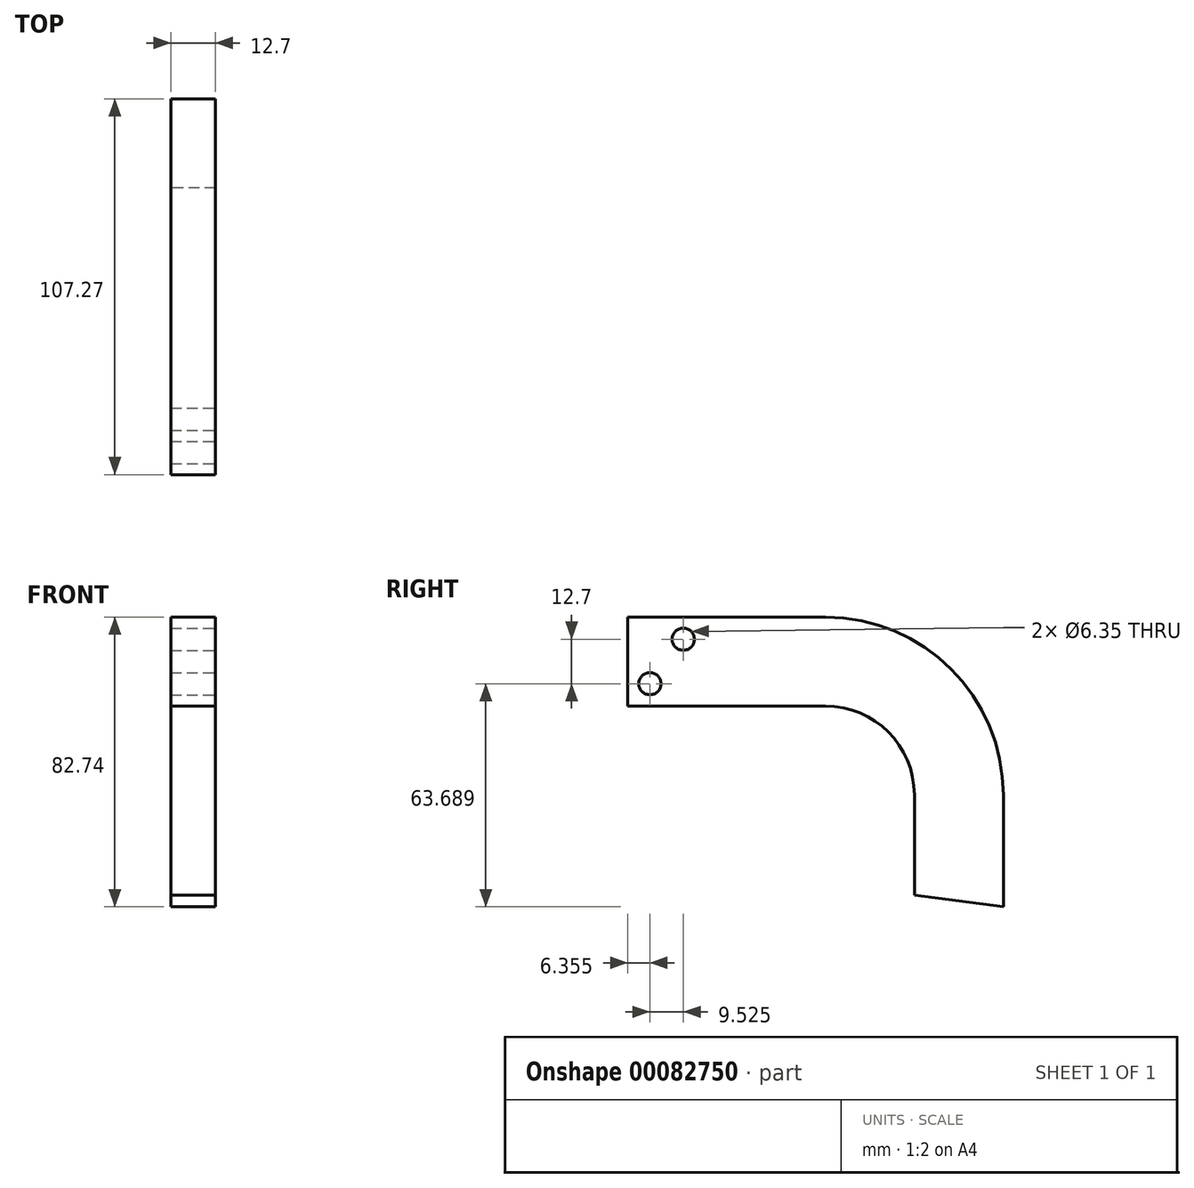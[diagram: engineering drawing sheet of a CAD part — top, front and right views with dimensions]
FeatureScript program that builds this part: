
annotation { "Feature Type Name" : "Feature", "Feature Type Description" : "" }
export const myFeature = defineFeature(function(context is Context, id is Id, definition is map)
    precondition{}
    {
        {
            var Q0;
            Q0=qCreatedBy(makeId("Right.planeOp"),FACE);
            var sketch = newSketch(context, id + "F0", { "sketchPlane" : qUnion([Q0])});
            skLineSegment(sketch, "E0.top", {"start": v(-57.14, 11.66) * mm, "end": v(-0.67, 11.66) * mm});
            skLineSegment(sketch, "E0.left", {"start": v(-57.14, 37.06) * mm, "end": v(-57.14, 11.66) * mm});
            skLineSegment(sketch, "E1", {"start": v(24.73, -13.74) * mm, "end": v(24.73, -42.32) * mm});
            skLineSegment(sketch, "E2", {"start": v(50.13, -45.68) * mm, "end": v(24.73, -42.32) * mm});
            skPoint(sketch, "E3.visualSharp", {"position": v(24.73, 11.66) * mm});
            skArc(sketch, "E3.filletArc", {"start": v(24.73, -13.74) * mm, "mid": v(17.29, 4.22) * mm, "end": v(-0.67, 11.66) * mm});
            skLineSegment(sketch, "E4.0", {"start": v(50.13, -13.74) * mm, "end": v(50.13, -45.68) * mm});
            skArc(sketch, "E4.1", {"start": v(50.13, -13.74) * mm, "mid": v(35.25, 22.18) * mm, "end": v(-0.67, 37.06) * mm});
            skLineSegment(sketch, "E4.2", {"start": v(-76.19, 37.06) * mm, "end": v(-0.67, 37.06) * mm});
            skPoint(sketch, "E5.orphan", {"position": v(69.18, -48.2) * mm});
            skSolve(sketch);
        }
        {
            var Q0;
            Q0=qSketchRegion(id+"F0",true);
            extrude(context, id + "F1", {"entities" : qUnion([Q0]), "depth" : 12.7 * mm});
        }
        {
            var Q0;
            Q0=makeQuery(id+"F1.opExtrude","CAP_FACE",FACE,{"disambiguationData":[OSD([sQuery(id+"F0.wireOp",EDGE,"E0.top"),sQuery(id+"F0.wireOp",EDGE,"E0.left"),sQuery(id+"F0.wireOp",EDGE,"E1"),sQuery(id+"F0.wireOp",EDGE,"E2"),sQuery(id+"F0.wireOp",EDGE,"E3.filletArc"),sQuery(id+"F0.wireOp",EDGE,"E4.0"),sQuery(id+"F0.wireOp",EDGE,"E4.1"),sQuery(id+"F0.wireOp",EDGE,"E4.2")])],"isStart":false});
            var sketch = newSketch(context, id + "F2", { "sketchPlane" : qUnion([Q0])});
            skCircle(sketch, "E6", {"center": v(-50.79, 18) * mm, "radius": 3.18 * mm});
            skCircle(sketch, "E7", {"center": v(-41.26, 30.7) * mm, "radius": 3.18 * mm});
            skSolve(sketch);
        }
        {
            var Q0;
            Q0=sQuery(id+"F2.wireOp",VERTEX,"E6.center");
            var Q1;
            Q1=sQuery(id+"F2.wireOp",VERTEX,"E7.center");
            var Q2;
            Q2=makeQuery(id+"F1.opExtrude","SWEPT_BODY",BODY,{"disambiguationData":[OSD([sQuery(id+"F0.wireOp",EDGE,"E0.top"),sQuery(id+"F0.wireOp",EDGE,"E0.left"),sQuery(id+"F0.wireOp",EDGE,"E1"),sQuery(id+"F0.wireOp",EDGE,"E2"),sQuery(id+"F0.wireOp",EDGE,"E3.filletArc"),sQuery(id+"F0.wireOp",EDGE,"E4.0"),sQuery(id+"F0.wireOp",EDGE,"E4.1"),sQuery(id+"F0.wireOp",EDGE,"E4.2")])]});
            hole(context, id + "F3", {"style" : HoleStyle.SIMPLE, "endStyle" : HoleEndStyle.THROUGH, "holeDiameter" : 6.35 * mm, "locations" : qUnion([Q0, Q1]), "scope" : qUnion([Q2]), "isTappedThrough" : true});
        }
    });
